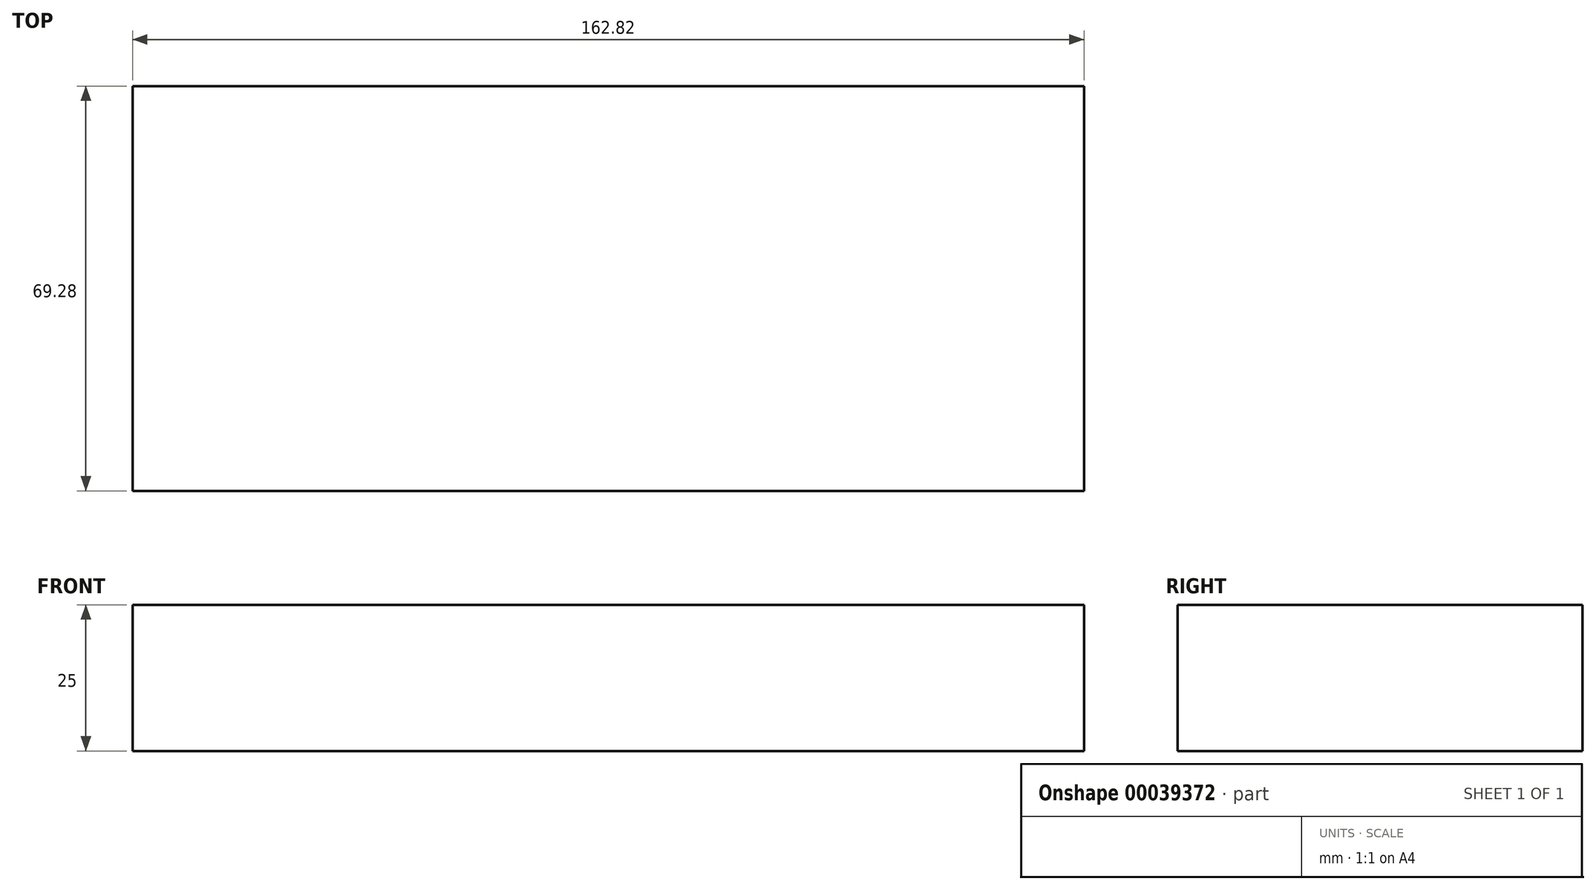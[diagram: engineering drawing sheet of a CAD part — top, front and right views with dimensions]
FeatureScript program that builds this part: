
annotation { "Feature Type Name" : "Feature", "Feature Type Description" : "" }
export const myFeature = defineFeature(function(context is Context, id is Id, definition is map)
    precondition{}
    {
        {
            var Q0;
            Q0=qCreatedBy(makeId("Top.planeOp"),FACE);
            var sketch = newSketch(context, id + "F0", { "sketchPlane" : qUnion([Q0])});
            skLineSegment(sketch, "E0.rect.bottom", {"start": v(-81.41, 34.64) * mm, "end": v(81.41, 34.64) * mm});
            skLineSegment(sketch, "E0.rect.top", {"start": v(-81.41, -34.64) * mm, "end": v(81.41, -34.64) * mm});
            skLineSegment(sketch, "E0.rect.left", {"start": v(-81.41, 34.64) * mm, "end": v(-81.41, -34.64) * mm});
            skLineSegment(sketch, "E0.rect.right", {"start": v(81.41, 34.64) * mm, "end": v(81.41, -34.64) * mm});
            skPoint(sketch, "E0.rect.middle", {"position": v(0, 0) * mm});
            skSolve(sketch);
        }
        {
            var Q0;
            Q0 = qSketchRegion(id + "F0", true);
            extrude(context, id + "F1", {"entities" : qUnion([Q0]), "depth" : 25 * mm});
        }
    });
